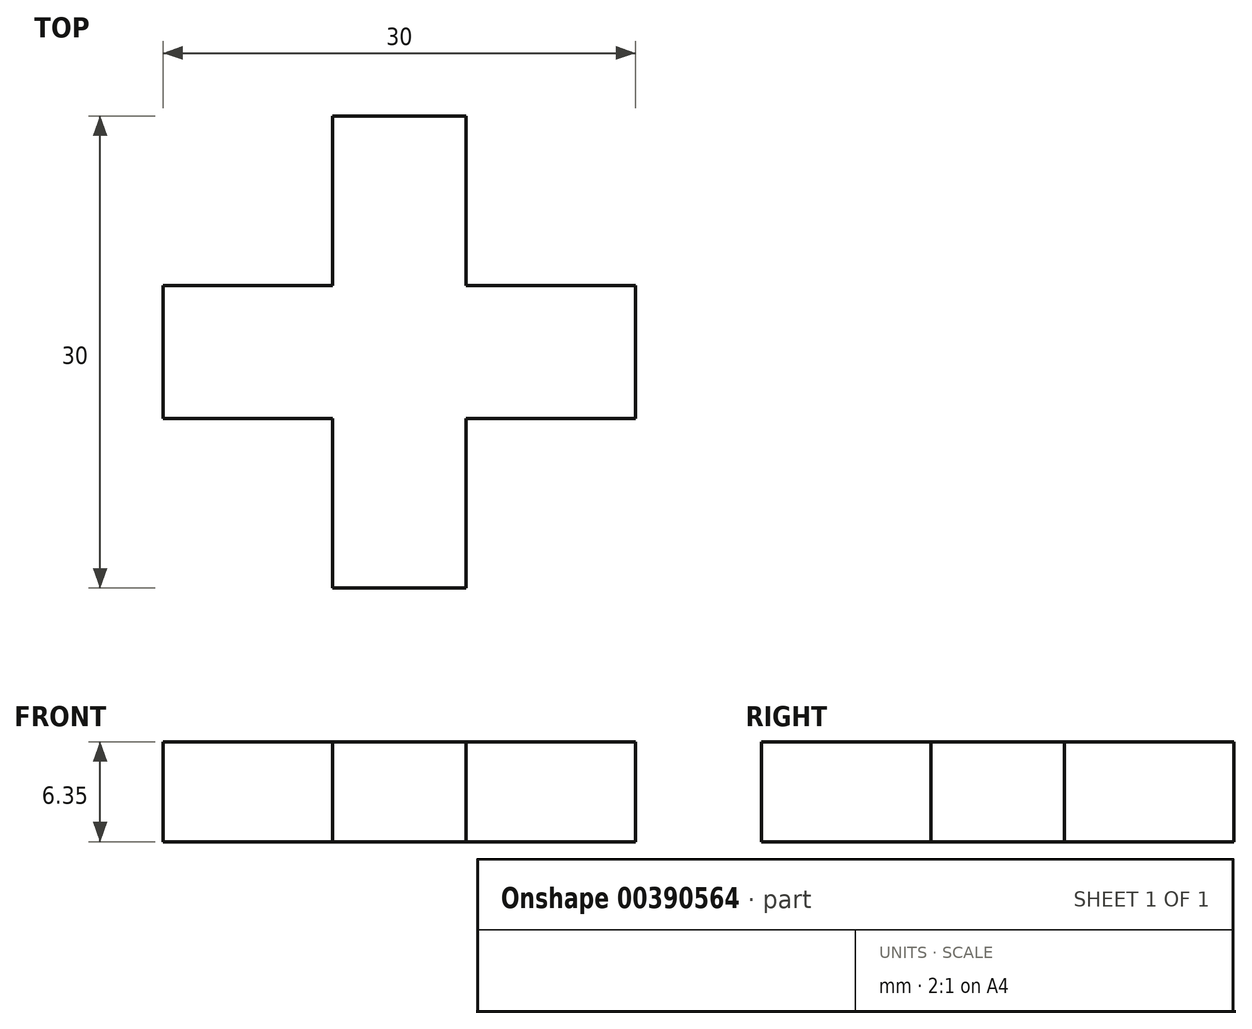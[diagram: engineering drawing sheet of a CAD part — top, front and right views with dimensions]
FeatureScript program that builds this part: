
annotation { "Feature Type Name" : "Feature", "Feature Type Description" : "" }
export const myFeature = defineFeature(function(context is Context, id is Id, definition is map)
    precondition{}
    {
        {
            var Q0;
            Q0=qCreatedBy(makeId("Top.planeOp"),FACE);
            var sketch = newSketch(context, id + "F0", { "sketchPlane" : qUnion([Q0])});
            skLineSegment(sketch, "E0.bottom", {"start": v(15, -15) * mm, "end": v(-15, -15) * mm, "construction": true});
            skLineSegment(sketch, "E0.top", {"start": v(15, 15) * mm, "end": v(-15, 15) * mm, "construction": true});
            skLineSegment(sketch, "E0.left", {"start": v(15, -15) * mm, "end": v(15, 15) * mm, "construction": true});
            skLineSegment(sketch, "E0.right", {"start": v(-15, -15) * mm, "end": v(-15, 15) * mm, "construction": true});
            skPoint(sketch, "E0.middle", {"position": v(0, 0) * mm});
            skLineSegment(sketch, "E1.bottom", {"start": v(4.23, -15) * mm, "end": v(-4.23, -15) * mm});
            skLineSegment(sketch, "E1.top", {"start": v(4.23, 15) * mm, "end": v(-4.23, 15) * mm});
            skLineSegment(sketch, "E1.left", {"start": v(4.23, -15) * mm, "end": v(4.23, -4.24) * mm});
            skLineSegment(sketch, "E1.right", {"start": v(-4.23, -15) * mm, "end": v(-4.23, -4.24) * mm});
            skLineSegment(sketch, "E2.bottom", {"start": v(15, -4.24) * mm, "end": v(4.23, -4.24) * mm});
            skLineSegment(sketch, "E2.top", {"start": v(15, 4.24) * mm, "end": v(4.23, 4.24) * mm});
            skLineSegment(sketch, "E2.left", {"start": v(15, -4.24) * mm, "end": v(15, 4.24) * mm});
            skLineSegment(sketch, "E2.right", {"start": v(-15, -4.24) * mm, "end": v(-15, 4.24) * mm});
            skLineSegment(sketch, "E3.trimOffspring", {"start": v(-4.23, 4.24) * mm, "end": v(-15, 4.24) * mm});
            skLineSegment(sketch, "E4.trimOffspring", {"start": v(4.23, 4.24) * mm, "end": v(4.23, 15) * mm});
            skLineSegment(sketch, "E5.trimOffspring", {"start": v(-4.23, -4.24) * mm, "end": v(-15, -4.24) * mm});
            skLineSegment(sketch, "E6.trimOffspring", {"start": v(-4.23, 4.24) * mm, "end": v(-4.23, 15) * mm});
            skSolve(sketch);
        }
        {
            var Q0;
            Q0=makeQuery(id+"F0.imprint","IMPRINT",FACE,{"disambiguationData":[TD([[makeQuery(id+"F0.imprint","IMPRINT",EDGE,{"derivedFrom":sQuery(id+"F0.wireOp",EDGE,"E1.bottom")}),-1.0]])]});
            extrude(context, id + "F1", {"entities" : qUnion([Q0]), "depth" : 6.35 * mm});
        }
    });
